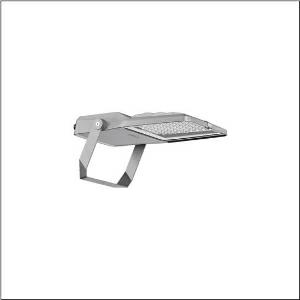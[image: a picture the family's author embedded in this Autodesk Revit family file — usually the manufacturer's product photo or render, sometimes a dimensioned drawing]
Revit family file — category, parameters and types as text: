
# Revit family: floodlight_fl_21_mini___pl43_5xa7774c4a1a_6312
name_source: partatom
category: Lighting Fixtures
units: mm (PartAtom-declared; Revit-internal decimal feet)

## family parameters
Cut with Voids When Loaded = No
Host = Face
Light Source = No
Part Type = Normal
Room Calculation Point = No
Round Connector Dimension = Use Diameter
Shared = No

## types (1)
- --- (1 x LED, 13000 lm, 88.8 W, 4000K)
    Apparent Load = 89 VA
    CIE Flux Codes = 27 78 99 100 100
    Color Rendering = 70
    Color Temperature = 4000K
    Default Elevation = 1800 mm
    Description = Floodlight FL 21 mini, floodlight, primary light control with lens, of PMMA, primary optical cover: protective disc, of toughened safety glass, transparent, light distribution: PL43, light emission: direct distribution, installation type: surface-mounted, LED, High Power LED, rated luminous flux: 13.000lm, luminous efficacy: 146lm/W, light colour: 740, colour temperature: 4000K, control gear: DALI 2, control: overheat protection, power reduction, constant luminous flux control, flexible luminous flux parameterisation, with terminal, 6-pole, mains connection: 220..240V, AC/DC, 0/50..60Hz, start of lifetime: 89W, end of service life: 94W, reduction: 42W, luminaire housing, of diecast aluminium, powder-coated, Siteco® metallic grey (DB 702S), corrosivity category C5 mid according to DIN EN ISO 12944, chlorine-resistant, suitable for swimming pools, sealing non-destructively replaceable, mounting bracket, of steel, galvanised, powder-coated, Siteco® metallic grey (DB 702S), protection rating (complete): IP66, insulation class (complete): insulation class II (safety insulation), certification: CE, ENEC, VDE, impact resistance: IK08, permissible operating ambient temperature: -40..+40°C, permissible operating ambient temperature for outdoor applications: -40..+50°C, standard: DIN EN 12944, LABS conformity tested according to VDMA 24364:2018-05, packaging unit: 1 piece

Light Distribution: PL43
    Height = 70 mm
    Lamp = 1 x LED
    Lamp Light Flux = 13000 lm
    Lamp Power = 88.8 W
    Lamp count = 1
    Length = 485 mm
    Luminous efficacy = 146 lm/W
    Manufacturer = Siteco
    ModVariant = No
    Model = 5XA7774C4A1A
    Number of Poles = 1
    OnlyDefault = Yes
    Power Factor = 1
    Product Name = Floodlight FL 21 mini | PL43
    Product group = floodlight | pylon annexe
    ProductGroupID = 6200
    Protection Class = Protection class II
    Protection Degree = IP 66
    RLX_Detail_Level = 1
    RLX_Emergency_Light_Flux = 0 lm
    RLX_Emergency_Type = 0
    RLX_Emergency_Type_DB = No
    RlxData = <blob elided: 95969 chars, md5=96b93659>
    Socket = socket
    Standby Power = 0 W
    System Light Flux = 13000 lm
    System Power = 89 W
    Type Comments = factory setting: luminous flux: 100 % | dim-lin: 254 | 456 mA
    Type Image = l_1006845.jpg
    URL = http://relux.com
    VarID = @adj_161550
    Voltage = 0 V
    Weight = 0.00 kg
    Width = 337 mm

## geometry (parser evidence)
native form markers: Blend x4, Sweep x12
no freeform markers — native parametric forms only
